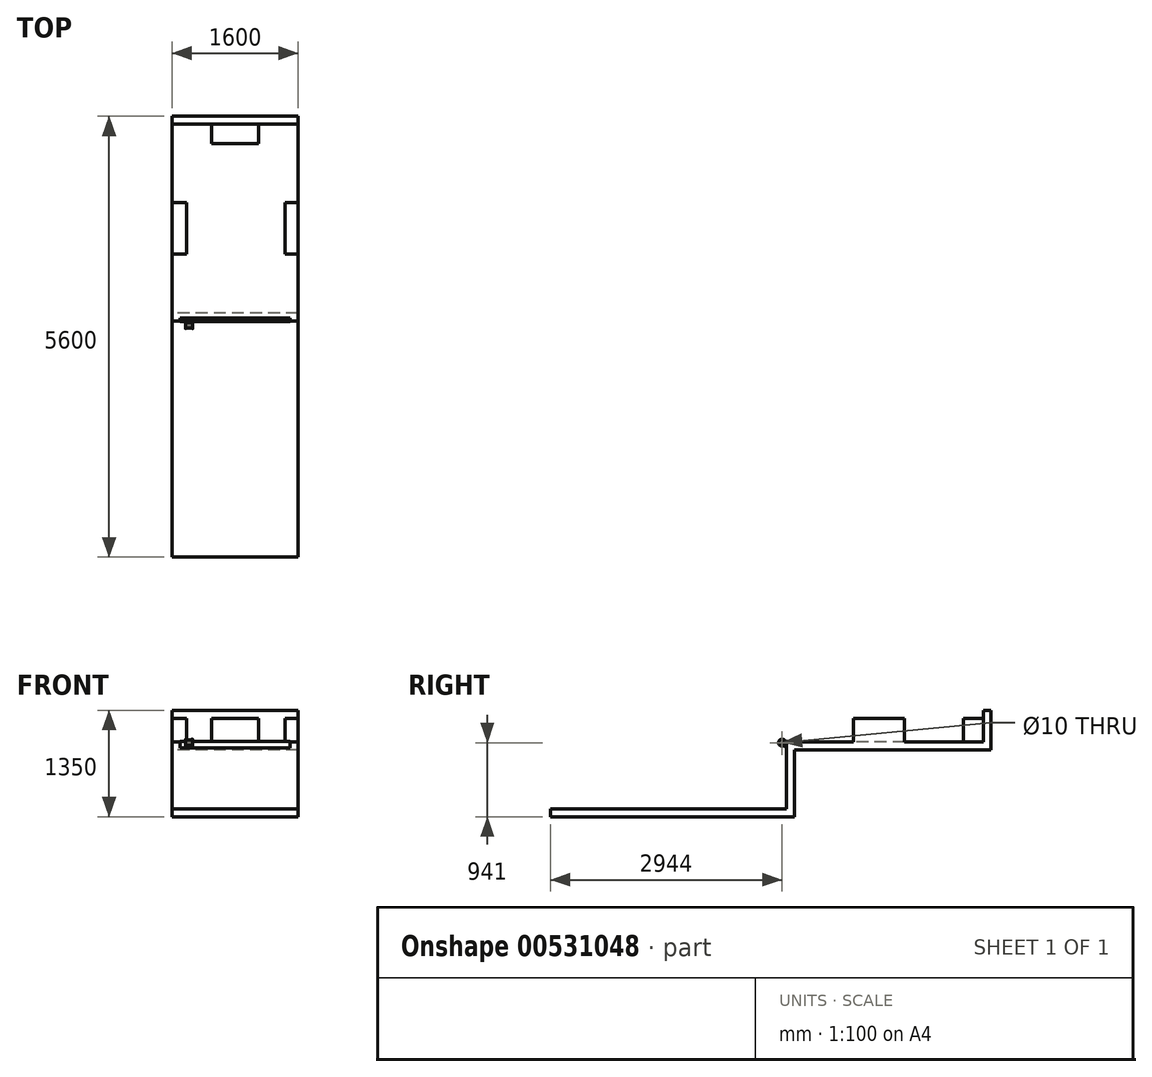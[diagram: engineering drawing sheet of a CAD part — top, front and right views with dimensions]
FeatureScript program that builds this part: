
annotation { "Feature Type Name" : "Feature", "Feature Type Description" : "" }
export const myFeature = defineFeature(function(context is Context, id is Id, definition is map)
    precondition{}
    {
        {
            var Q0;
            Q0=qCreatedBy(makeId("Right.planeOp"),FACE);
            var sketch = newSketch(context, id + "F0", { "sketchPlane" : qUnion([Q0])});
            skLineSegment(sketch, "E0", {"start": v(-3000, 0) * mm, "end": v(0, 0) * mm});
            skLineSegment(sketch, "E1", {"start": v(0, 0) * mm, "end": v(0, 850) * mm});
            skLineSegment(sketch, "E2", {"start": v(0, 850) * mm, "end": v(2500, 850) * mm});
            skLineSegment(sketch, "E3", {"start": v(2500, 850) * mm, "end": v(2500, 1250) * mm});
            skLineSegment(sketch, "E4.0", {"start": v(2600, 750) * mm, "end": v(2600, 1250) * mm});
            skLineSegment(sketch, "E4.1", {"start": v(100, 750) * mm, "end": v(2600, 750) * mm});
            skLineSegment(sketch, "E4.2", {"start": v(100, -100) * mm, "end": v(100, 750) * mm});
            skLineSegment(sketch, "E4.3", {"start": v(-3000, -100) * mm, "end": v(100, -100) * mm});
            skLineSegment(sketch, "E5", {"start": v(-3000, 0) * mm, "end": v(-3000, -100) * mm});
            skLineSegment(sketch, "E6", {"start": v(2500, 1250) * mm, "end": v(2600, 1250) * mm});
            skSolve(sketch);
        }
        {
            var Q0;
            Q0=makeQuery(id+"F0.imprint","IMPRINT",FACE,{"disambiguationData":[TD([[makeQuery(id+"F0.imprint","IMPRINT",EDGE,{"derivedFrom":sQuery(id+"F0.wireOp",EDGE,"E0")}),-1.0]])]});
            extrude(context, id + "F1", {"entities" : qUnion([Q0]), "endBound" : BoundingType.SYMMETRIC, "depth" : 1600 * mm, "offsetDistance" : 25 * mm});
        }
        {
            var Q0;
            Q0=makeQuery(id+"F1.opExtrude","SWEPT_FACE",FACE,{"disambiguationData":[OSD([sQuery(id+"F0.wireOp",EDGE,"E2")])]});
            var sketch = newSketch(context, id + "F2", { "sketchPlane" : qUnion([Q0])});
            skLineSegment(sketch, "E7.bottom", {"start": v(-800, 1500) * mm, "end": v(-615, 1500) * mm});
            skLineSegment(sketch, "E7.top", {"start": v(-800, 850) * mm, "end": v(-615, 850) * mm});
            skLineSegment(sketch, "E7.left", {"start": v(-800, 1500) * mm, "end": v(-800, 850) * mm});
            skLineSegment(sketch, "E7.right", {"start": v(-615, 1500) * mm, "end": v(-615, 850) * mm});
            skLineSegment(sketch, "E8.bottom", {"start": v(800, 1500) * mm, "end": v(635, 1500) * mm});
            skLineSegment(sketch, "E8.top", {"start": v(800, 850) * mm, "end": v(635, 850) * mm});
            skLineSegment(sketch, "E8.left", {"start": v(800, 1500) * mm, "end": v(800, 850) * mm});
            skLineSegment(sketch, "E8.right", {"start": v(635, 1500) * mm, "end": v(635, 850) * mm});
            skLineSegment(sketch, "E9.bottom", {"start": v(-300, 2500) * mm, "end": v(300, 2500) * mm});
            skLineSegment(sketch, "E9.top", {"start": v(-300, 2250) * mm, "end": v(300, 2250) * mm});
            skLineSegment(sketch, "E9.left", {"start": v(-300, 2500) * mm, "end": v(-300, 2250) * mm});
            skLineSegment(sketch, "E9.right", {"start": v(300, 2500) * mm, "end": v(300, 2250) * mm});
            skLineSegment(sketch, "E10", {"start": v(0, 2250) * mm, "end": v(0, 0) * mm, "construction": true});
            skPoint(sketch, "E11", {"position": v(0, 2250) * mm});
            skSolve(sketch);
        }
        {
            var Q0;
            Q0=makeQuery(id+"F2.imprint","IMPRINT",FACE,{"disambiguationData":[TD([[makeQuery(id+"F2.imprint","IMPRINT",EDGE,{"derivedFrom":sQuery(id+"F2.wireOp",EDGE,"E7.bottom")}),-1.0]])]});
            var Q1;
            Q1=makeQuery(id+"F2.imprint","IMPRINT",FACE,{"disambiguationData":[TD([[makeQuery(id+"F2.imprint","IMPRINT",EDGE,{"derivedFrom":sQuery(id+"F2.wireOp",EDGE,"E8.bottom")}),1.0]])]});
            var Q2;
            Q2=makeQuery(id+"F2.imprint","IMPRINT",FACE,{"disambiguationData":[TD([[makeQuery(id+"F2.imprint","IMPRINT",EDGE,{"derivedFrom":sQuery(id+"F2.wireOp",EDGE,"E9.bottom")}),1.0]])]});
            extrude(context, id + "F3", {"entities" : qUnion([Q0, Q1, Q2]), "operationType" : NewBodyOperationType.ADD, "depth" : 300 * mm, "offsetDistance" : 25 * mm});
        }
        {
            var Q0;
            Q0=qCreatedBy(makeId("Right.planeOp"),FACE);
            var sketch = newSketch(context, id + "F4", { "sketchPlane" : qUnion([Q0])});
            skLineSegment(sketch, "E12", {"start": v(0, 850) * mm, "end": v(34, 850) * mm});
            skLineSegment(sketch, "E13", {"start": v(34, 850) * mm, "end": v(34, 856) * mm});
            skLineSegment(sketch, "E14", {"start": v(34, 856) * mm, "end": v(-6, 856) * mm});
            skLineSegment(sketch, "E15", {"start": v(-6, 856) * mm, "end": v(-6, 776) * mm});
            skLineSegment(sketch, "E16", {"start": v(-6, 776) * mm, "end": v(0, 776) * mm});
            skLineSegment(sketch, "E17", {"start": v(0, 776) * mm, "end": v(0, 850) * mm});
            skSolve(sketch);
        }
        {
            var Q0;
            Q0=makeQuery(id+"F4.imprint","IMPRINT",FACE,{"disambiguationData":[TD([[makeQuery(id+"F4.imprint","IMPRINT",EDGE,{"derivedFrom":sQuery(id+"F4.wireOp",EDGE,"E12")}),1.0]])]});
            extrude(context, id + "F5", {"entities" : qUnion([Q0]), "endBound" : BoundingType.SYMMETRIC, "depth" : 1400 * mm, "offsetDistance" : 25 * mm});
        }
        {
            var Q0;
            Q0=makeQuery(id+"F5.opExtrude","SWEPT_FACE",FACE,{"disambiguationData":[OSD([sQuery(id+"F4.wireOp",EDGE,"E15")])]});
            cPlane(context, id + "F6", {"entities" : qUnion([Q0]), "cplaneType" : CPlaneType.OFFSET, "offset" : 50 * mm, "width" : 150 * mm, "height" : 150 * mm});
        }
        {
            var Q0;
            Q0=qCreatedBy(id+"F6.planeOp",FACE);
            var sketch = newSketch(context, id + "F7", { "sketchPlane" : qUnion([Q0])});
            skLineSegment(sketch, "E18", {"start": v(-627.67, 885.88) * mm, "end": v(-600.68, 876.12) * mm});
            skLineSegment(sketch, "E19", {"start": v(-600, 876) * mm, "end": v(-570.7, 876) * mm});
            skLineSegment(sketch, "E20", {"start": v(-570.02, 876.12) * mm, "end": v(-543.03, 885.88) * mm});
            skLineSegment(sketch, "E21", {"start": v(-540.35, 884) * mm, "end": v(-540.35, 846) * mm});
            skLineSegment(sketch, "E22", {"start": v(-540.35, 846) * mm, "end": v(-630.35, 846) * mm});
            skLineSegment(sketch, "E23", {"start": v(-630.35, 846) * mm, "end": v(-630.35, 884) * mm});
            skPoint(sketch, "E24.visualSharp", {"position": v(-630.35, 886.85) * mm});
            skArc(sketch, "E24.filletArc", {"start": v(-627.67, 885.88) * mm, "mid": v(-629.5, 885.64) * mm, "end": v(-630.35, 884) * mm});
            skPoint(sketch, "E25.visualSharp", {"position": v(-540.35, 886.85) * mm});
            skArc(sketch, "E25.filletArc", {"start": v(-540.35, 884) * mm, "mid": v(-541.2, 885.64) * mm, "end": v(-543.03, 885.88) * mm});
            skPoint(sketch, "E26.visualSharp", {"position": v(-600.35, 876) * mm});
            skArc(sketch, "E26.filletArc", {"start": v(-600.68, 876.12) * mm, "mid": v(-600.35, 876.03) * mm, "end": v(-600, 876) * mm});
            skPoint(sketch, "E27.visualSharp", {"position": v(-570.35, 876) * mm});
            skArc(sketch, "E27.filletArc", {"start": v(-570.7, 876) * mm, "mid": v(-570.36, 876.03) * mm, "end": v(-570.02, 876.12) * mm});
            skLineSegment(sketch, "E28", {"start": v(-607.11, 886) * mm, "end": v(-535.15, 886) * mm, "construction": true});
            skPoint(sketch, "E29", {"position": v(-585.35, 876) * mm});
            skLineSegment(sketch, "E30", {"start": v(-620.42, 841) * mm, "end": v(-524.5, 841) * mm, "construction": true});
            skLineSegment(sketch, "E31", {"start": v(0, 0) * mm, "end": v(0, 2102.2) * mm, "construction": true});
            skArc(sketch, "E32.MirrorCS", {"start": v(600.68, 876.12) * mm, "mid": v(600.35, 876.03) * mm, "end": v(600, 876) * mm});
            skLineSegment(sketch, "E33.MirrorCS", {"start": v(627.67, 885.88) * mm, "end": v(600.68, 876.12) * mm});
            skLineSegment(sketch, "E34.MirrorCS", {"start": v(570.02, 876.12) * mm, "end": v(543.03, 885.88) * mm});
            skArc(sketch, "E35.MirrorCS", {"start": v(627.67, 885.88) * mm, "mid": v(629.5, 885.64) * mm, "end": v(630.35, 884) * mm});
            skLineSegment(sketch, "E36.MirrorCS", {"start": v(540.35, 884) * mm, "end": v(540.35, 846) * mm});
            skArc(sketch, "E37.MirrorCS", {"start": v(570.7, 876) * mm, "mid": v(570.36, 876.03) * mm, "end": v(570.02, 876.12) * mm});
            skLineSegment(sketch, "E38.MirrorCS", {"start": v(600, 876) * mm, "end": v(570.7, 876) * mm});
            skArc(sketch, "E39.MirrorCS", {"start": v(540.35, 884) * mm, "mid": v(541.2, 885.64) * mm, "end": v(543.03, 885.88) * mm});
            skLineSegment(sketch, "E40.MirrorCS", {"start": v(540.35, 846) * mm, "end": v(630.35, 846) * mm});
            skLineSegment(sketch, "E41.MirrorCS", {"start": v(630.35, 846) * mm, "end": v(630.35, 884) * mm});
            skLineSegment(sketch, "E42.MirrorCS", {"start": v(607.11, 886) * mm, "end": v(535.15, 886) * mm, "construction": true});
            skLineSegment(sketch, "E43.MirrorCS", {"start": v(620.42, 841) * mm, "end": v(524.5, 841) * mm, "construction": true});
            skPoint(sketch, "E44.MirrorP", {"position": v(585.35, 876) * mm});
            skPoint(sketch, "E45.MirrorP", {"position": v(600.35, 876) * mm});
            skPoint(sketch, "E46.MirrorP", {"position": v(540.35, 886.85) * mm});
            skPoint(sketch, "E47.MirrorP", {"position": v(570.35, 876) * mm});
            skPoint(sketch, "E48.MirrorP", {"position": v(630.35, 886.85) * mm});
            skSolve(sketch);
        }
        {
            var Q0;
            Q0=makeQuery(id+"F7.imprint","IMPRINT",FACE,{"disambiguationData":[TD([[makeQuery(id+"F7.imprint","IMPRINT",EDGE,{"derivedFrom":sQuery(id+"F7.wireOp",EDGE,"E18")}),-1.0]])]});
            var Q1;
            Q1=makeQuery(id+"F7.imprint","IMPRINT",FACE,{"disambiguationData":[TD([[makeQuery(id+"F7.imprint","IMPRINT",EDGE,{"derivedFrom":sQuery(id+"F7.wireOp",EDGE,"E32.MirrorCS")}),1.0]])]});
            var Q2;
            Q2=sQuery(id+"F7.wireOp",EDGE,"E43.MirrorCS");
            revolve(context, id + "F8", {"entities" : qUnion([Q0, Q1]), "axis" : qUnion([Q2]), "revolveType" : RevolveType.FULL});
        }
    });
